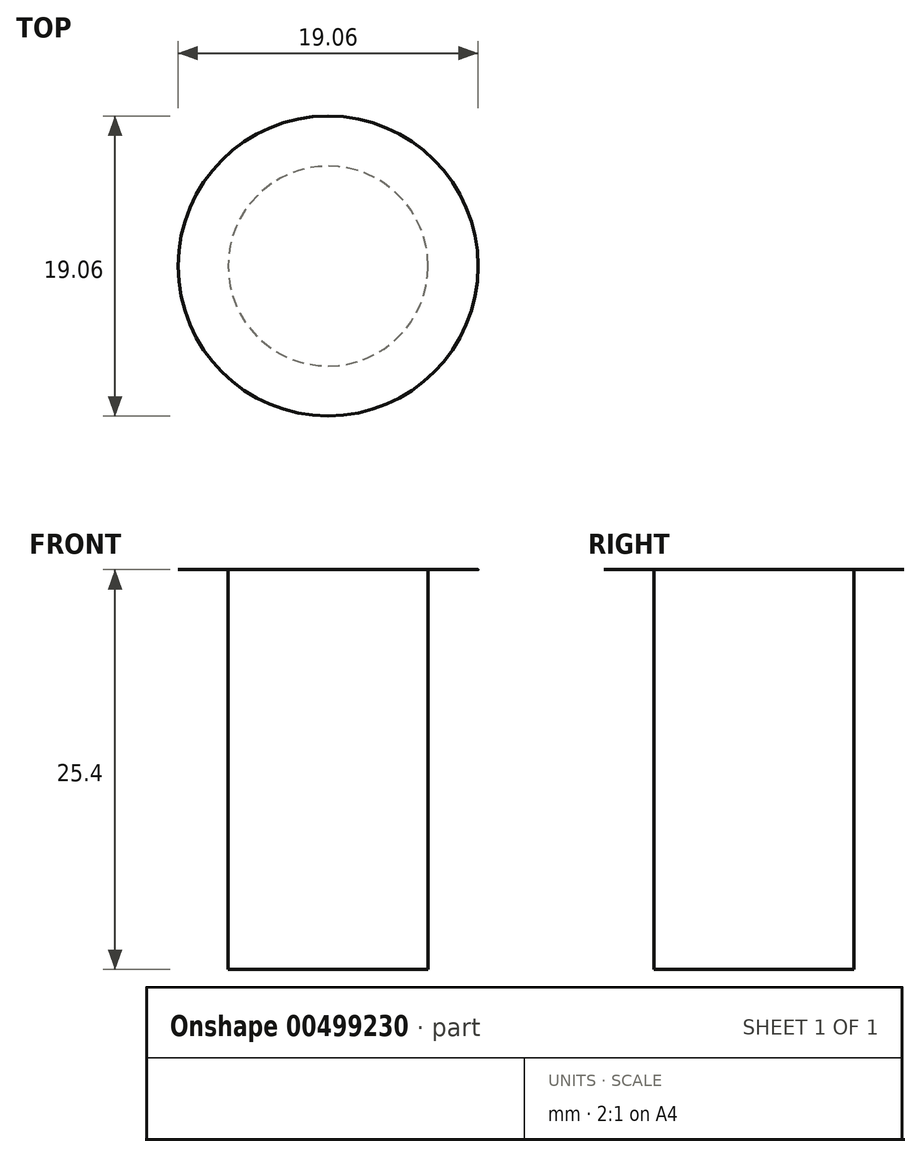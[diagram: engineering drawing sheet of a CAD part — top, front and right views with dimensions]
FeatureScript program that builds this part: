
annotation { "Feature Type Name" : "Feature", "Feature Type Description" : "" }
export const myFeature = defineFeature(function(context is Context, id is Id, definition is map)
    precondition{}
    {
        {
            var Q0;
            Q0=qCreatedBy(makeId("Top.planeOp"),FACE);
            var sketch = newSketch(context, id + "F0", { "sketchPlane" : qUnion([Q0])});
            skCircle(sketch, "E0", {"center": v(0, 0) * mm, "radius": 9.53 * mm});
            skSolve(sketch);
        }
        {
            var Q0;
            Q0 = qSketchRegion(id + "F0", true);
            extrude(context, id + "F1", {"entities" : qUnion([Q0]), "depth" : 1 / 406.4 * mm, "offsetDistance" : 25.4 * mm});
        }
        {
            var Q0;
            Q0=makeQuery(id+"F1.opExtrude","CAP_FACE",FACE,{"disambiguationData":[OSD([sQuery(id+"F0.wireOp",EDGE,"E0")])],"isStart":true});
            var sketch = newSketch(context, id + "F2", { "sketchPlane" : qUnion([Q0])});
            skCircle(sketch, "E1", {"center": v(0, 0) * mm, "radius": 6.35 * mm});
            skSolve(sketch);
        }
        {
            var Q0;
            Q0 = qSketchRegion(id + "F2", true);
            extrude(context, id + "F3", {"entities" : qUnion([Q0]), "operationType" : NewBodyOperationType.ADD, "depth" : 25.4 * mm, "offsetDistance" : 25.4 * mm});
        }
    });
